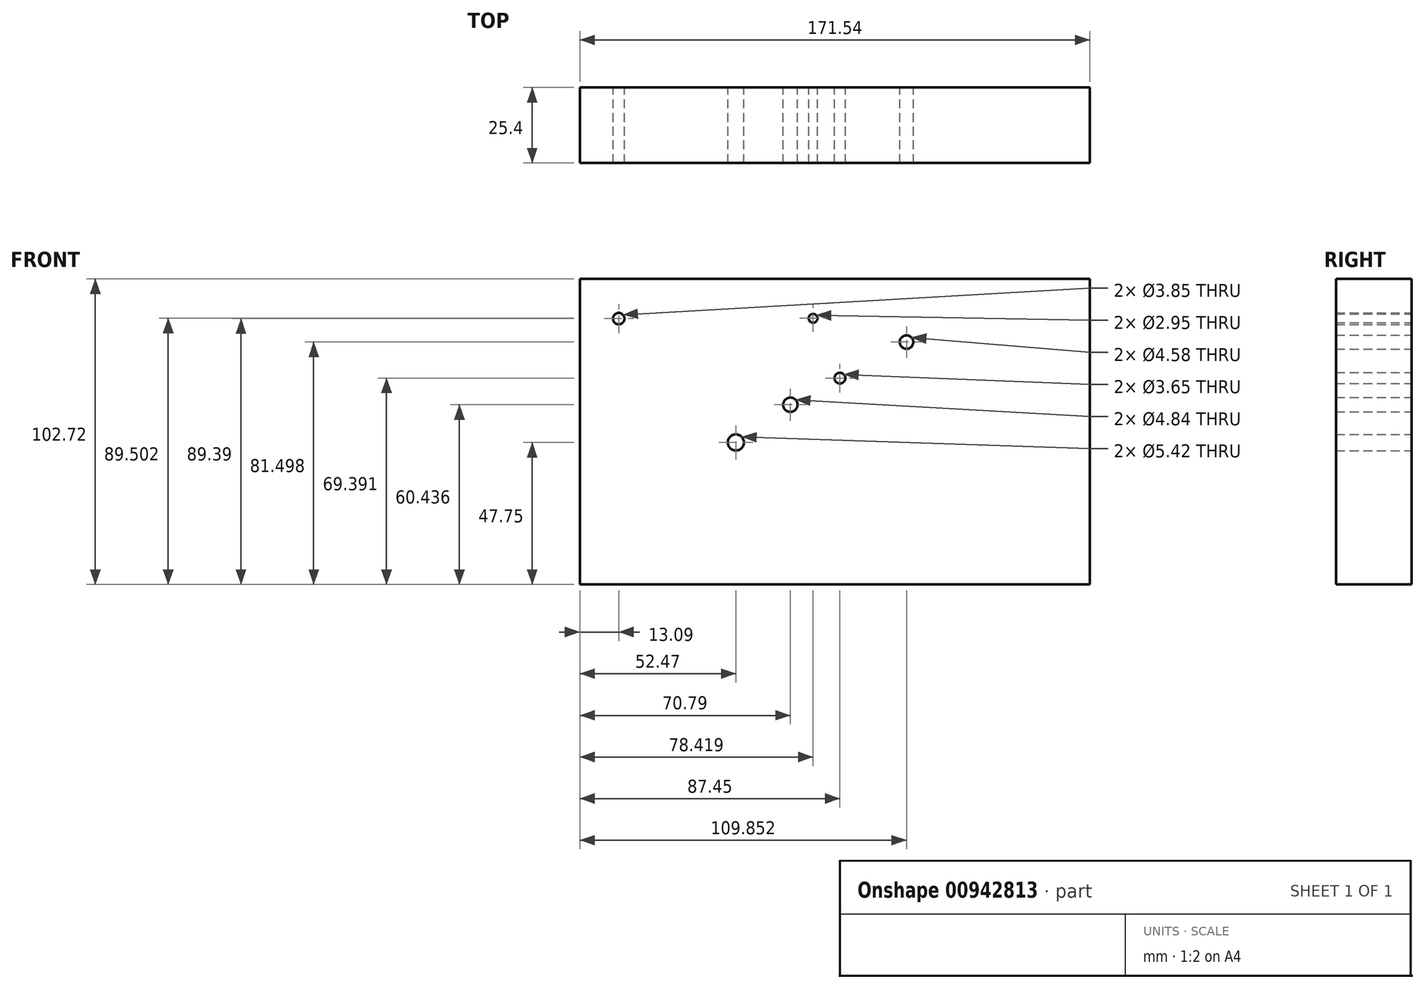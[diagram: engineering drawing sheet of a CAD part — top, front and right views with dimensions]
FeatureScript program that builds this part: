
annotation { "Feature Type Name" : "Feature", "Feature Type Description" : "" }
export const myFeature = defineFeature(function(context is Context, id is Id, definition is map)
    precondition{}
    {
        {
            var Q0;
            Q0=qCreatedBy(makeId("Front.planeOp"),FACE);
            var sketch = newSketch(context, id + "F0", { "sketchPlane" : qUnion([Q0])});
            skLineSegment(sketch, "E0", {"start": v(-113.72, 57.52) * mm, "end": v(-113.72, -47.75) * mm});
            skLineSegment(sketch, "E1", {"start": v(-113.72, -47.75) * mm, "end": v(57.82, -47.75) * mm});
            skLineSegment(sketch, "E2", {"start": v(57.82, -47.75) * mm, "end": v(57.82, 54.97) * mm});
            skLineSegment(sketch, "E3", {"start": v(57.82, 54.97) * mm, "end": v(-113.72, 54.97) * mm});
            skCircle(sketch, "E4", {"center": v(-100.63, 41.64) * mm, "radius": 1.93 * mm});
            skCircle(sketch, "E5", {"center": v(-35.3, 41.75) * mm, "radius": 1.48 * mm});
            skCircle(sketch, "E6", {"center": v(-3.87, 33.75) * mm, "radius": 2.29 * mm});
            skCircle(sketch, "E7", {"center": v(-26.27, 21.64) * mm, "radius": 1.82 * mm});
            skCircle(sketch, "E8", {"center": v(-42.93, 12.69) * mm, "radius": 2.42 * mm});
            skCircle(sketch, "E9", {"center": v(-61.25, 0) * mm, "radius": 2.7 * mm});
            skSolve(sketch);
        }
        {
            var Q0;
            {var subQ1=sQuery(id+"F0.wireOp",EDGE,"E1");Q0=makeQuery(id+"F0.imprint","IMPRINT",FACE,{"disambiguationData":[TD([[makeQuery(id+"F0.imprint","IMPRINT",EDGE,{"derivedFrom":subQ1}),1.0]])]});}
            extrude(context, id + "F1", {"entities" : qUnion([Q0]), "depth" : 25.4 * mm, "offsetDistance" : 25.4 * mm});
        }
    });
